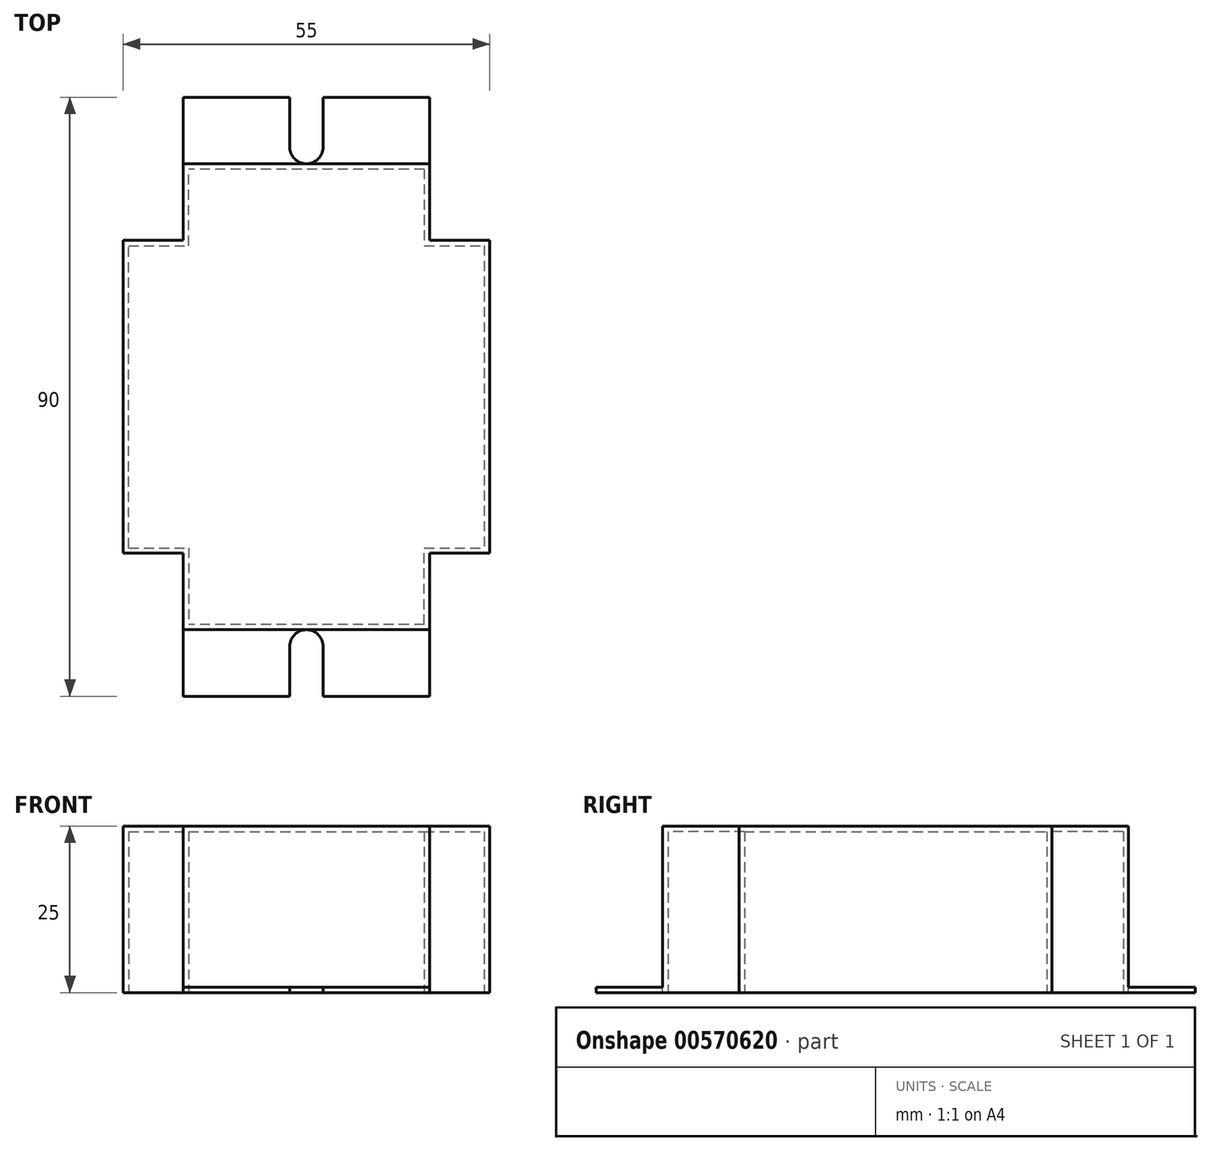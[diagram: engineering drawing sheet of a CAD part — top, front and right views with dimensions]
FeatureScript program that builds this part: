
annotation { "Feature Type Name" : "Feature", "Feature Type Description" : "" }
export const myFeature = defineFeature(function(context is Context, id is Id, definition is map)
    precondition{}
    {
        {
            var Q0;
            Q0=qCreatedBy(makeId("Top.planeOp"),FACE);
            var sketch = newSketch(context, id + "F0", { "sketchPlane" : qUnion([Q0])});
            skLineSegment(sketch, "E0", {"start": v(-33.6, -23.5) * mm, "end": v(-33.6, 23.5) * mm});
            skLineSegment(sketch, "E1", {"start": v(-33.6, 23.5) * mm, "end": v(-24.6, 23.5) * mm});
            skLineSegment(sketch, "E2", {"start": v(-24.6, 23.5) * mm, "end": v(-24.6, 35) * mm});
            skLineSegment(sketch, "E3", {"start": v(-24.6, 35) * mm, "end": v(12.4, 35) * mm});
            skLineSegment(sketch, "E4", {"start": v(12.4, 35) * mm, "end": v(12.4, 23.5) * mm});
            skLineSegment(sketch, "E5", {"start": v(12.4, 23.5) * mm, "end": v(21.4, 23.5) * mm});
            skLineSegment(sketch, "E6", {"start": v(21.4, 23.5) * mm, "end": v(21.4, -23.5) * mm});
            skLineSegment(sketch, "E7", {"start": v(35.03, 0) * mm, "end": v(-45.05, 0) * mm, "construction": true});
            skLineSegment(sketch, "E8.MirrorCS", {"start": v(-24.6, -35) * mm, "end": v(12.4, -35) * mm});
            skLineSegment(sketch, "E9.MirrorCS", {"start": v(12.4, -35) * mm, "end": v(12.4, -23.5) * mm});
            skLineSegment(sketch, "E10.MirrorCS", {"start": v(-33.6, -23.5) * mm, "end": v(-24.6, -23.5) * mm});
            skLineSegment(sketch, "E11.MirrorCS", {"start": v(-24.6, -23.5) * mm, "end": v(-24.6, -35) * mm});
            skLineSegment(sketch, "E12.MirrorCS", {"start": v(12.4, -23.5) * mm, "end": v(21.4, -23.5) * mm});
            skPoint(sketch, "E13.orphan", {"position": v(-33.6, 0) * mm});
            skPoint(sketch, "E14.orphan", {"position": v(21.4, 0) * mm});
            skSolve(sketch);
        }
        {
            var Q0;
            Q0=makeQuery(id+"F0.imprint","IMPRINT",FACE,{"disambiguationData":[TD([[makeQuery(id+"F0.imprint","IMPRINT",EDGE,{"derivedFrom":sQuery(id+"F0.wireOp",EDGE,"E0")}),-1.0]])]});
            extrude(context, id + "F1", {"entities" : qUnion([Q0]), "depth" : 25 * mm, "offsetDistance" : 25 * mm});
        }
        {
            var Q0;
            Q0=makeQuery(id+"F1.opExtrude","SWEPT_FACE",FACE,{"disambiguationData":[OSD([sQuery(id+"F0.wireOp",EDGE,"E8.MirrorCS")])]});
            var sketch = newSketch(context, id + "F2", { "sketchPlane" : qUnion([Q0])});
            skLineSegment(sketch, "E15.bottom", {"start": v(12.4, 0) * mm, "end": v(-24.6, 0) * mm});
            skLineSegment(sketch, "E15.top", {"start": v(12.4, 0.8) * mm, "end": v(-24.6, 0.8) * mm});
            skLineSegment(sketch, "E15.left", {"start": v(12.4, 0) * mm, "end": v(12.4, 0.8) * mm});
            skLineSegment(sketch, "E15.right", {"start": v(-24.6, 0) * mm, "end": v(-24.6, 0.8) * mm});
            skSolve(sketch);
        }
        {
            var Q0;
            Q0 = qSketchRegion(id + "F2", true);
            extrude(context, id + "F3", {"entities" : qUnion([Q0]), "operationType" : NewBodyOperationType.ADD, "depth" : 10 * mm, "offsetDistance" : 25 * mm});
        }
        {
            var Q0;
            Q0=makeQuery(id+"F1.opExtrude","SWEPT_FACE",FACE,{"disambiguationData":[OSD([sQuery(id+"F0.wireOp",EDGE,"E3")])]});
            var sketch = newSketch(context, id + "F4", { "sketchPlane" : qUnion([Q0])});
            skLineSegment(sketch, "E16.bottom", {"start": v(-12.4, 0) * mm, "end": v(24.6, 0) * mm});
            skLineSegment(sketch, "E16.top", {"start": v(-12.4, 0.8) * mm, "end": v(24.6, 0.8) * mm});
            skLineSegment(sketch, "E16.left", {"start": v(-12.4, 0) * mm, "end": v(-12.4, 0.8) * mm});
            skLineSegment(sketch, "E16.right", {"start": v(24.6, 0) * mm, "end": v(24.6, 0.8) * mm});
            skSolve(sketch);
        }
        {
            var Q0;
            Q0 = qSketchRegion(id + "F4", true);
            extrude(context, id + "F5", {"entities" : qUnion([Q0]), "operationType" : NewBodyOperationType.ADD, "depth" : 10 * mm, "offsetDistance" : 25 * mm});
        }
        {
            var Q0;
            Q0=makeQuery(id+"F5.boolean.opBoolean","MERGE",FACE,{"derivedFrom":[makeQuery(id+"F3.boolean.opBoolean","MERGE",FACE,{"derivedFrom":[makeQuery(id+"F1.opExtrude","CAP_FACE",FACE,{"disambiguationData":[OSD([sQuery(id+"F0.wireOp",EDGE,"E0"),sQuery(id+"F0.wireOp",EDGE,"E1"),sQuery(id+"F0.wireOp",EDGE,"E2"),sQuery(id+"F0.wireOp",EDGE,"E3"),sQuery(id+"F0.wireOp",EDGE,"E4"),sQuery(id+"F0.wireOp",EDGE,"E5"),sQuery(id+"F0.wireOp",EDGE,"E6"),sQuery(id+"F0.wireOp",EDGE,"E8.MirrorCS"),sQuery(id+"F0.wireOp",EDGE,"E9.MirrorCS"),sQuery(id+"F0.wireOp",EDGE,"E10.MirrorCS"),sQuery(id+"F0.wireOp",EDGE,"E11.MirrorCS"),sQuery(id+"F0.wireOp",EDGE,"E12.MirrorCS")])],"isStart":true}),makeQuery(id+"F3.opExtrude","SWEPT_FACE",FACE,{"disambiguationData":[OSD([sQuery(id+"F2.wireOp",EDGE,"E15.bottom")])]})]}),makeQuery(id+"F5.opExtrude","SWEPT_FACE",FACE,{"disambiguationData":[OSD([sQuery(id+"F4.wireOp",EDGE,"E16.bottom")])]})]});
            shell(context, id + "F6", {"entities" : qUnion([Q0]), "thickness" : 0.8 * mm});
        }
        {
            var Q0;
            Q0=makeQuery(id+"F5.opExtrude","SWEPT_FACE",FACE,{"disambiguationData":[OSD([sQuery(id+"F4.wireOp",EDGE,"E16.top")])]});
            var sketch = newSketch(context, id + "F7", { "sketchPlane" : qUnion([Q0])});
            skLineSegment(sketch, "E17.top", {"start": v(-3.6, 45) * mm, "end": v(-8.6, 45) * mm});
            skLineSegment(sketch, "E17.left", {"start": v(-3.6, 37.5) * mm, "end": v(-3.6, 45) * mm});
            skLineSegment(sketch, "E17.right", {"start": v(-8.6, 37.5) * mm, "end": v(-8.6, 45) * mm});
            skArc(sketch, "E18", {"start": v(-8.6, 37.5) * mm, "mid": v(-6.1, 35) * mm, "end": v(-3.6, 37.5) * mm});
            skSolve(sketch);
        }
        {
            var Q0;
            Q0=makeQuery(id+"F3.opExtrude","SWEPT_FACE",FACE,{"disambiguationData":[OSD([sQuery(id+"F2.wireOp",EDGE,"E15.top")])]});
            var sketch = newSketch(context, id + "F8", { "sketchPlane" : qUnion([Q0])});
            skLineSegment(sketch, "E19.top", {"start": v(-8.6, -45) * mm, "end": v(-3.6, -45) * mm});
            skLineSegment(sketch, "E19.left", {"start": v(-8.6, -37.5) * mm, "end": v(-8.6, -45) * mm});
            skLineSegment(sketch, "E19.right", {"start": v(-3.6, -37.5) * mm, "end": v(-3.6, -45) * mm});
            skArc(sketch, "E20", {"start": v(-3.6, -37.5) * mm, "mid": v(-6.1, -35) * mm, "end": v(-8.6, -37.5) * mm});
            skSolve(sketch);
        }
        {
            var Q0;
            Q0=makeQuery(id+"F8.imprint","IMPRINT",FACE,{"disambiguationData":[TD([[makeQuery(id+"F8.imprint","IMPRINT",EDGE,{"derivedFrom":sQuery(id+"F8.wireOp",EDGE,"E19.top")}),-1.0]])]});
            var Q1;
            Q1=makeQuery(id+"F7.imprint","IMPRINT",FACE,{"disambiguationData":[TD([[makeQuery(id+"F7.imprint","IMPRINT",EDGE,{"derivedFrom":sQuery(id+"F7.wireOp",EDGE,"E17.top")}),1.0]])]});
            extrude(context, id + "F9", {"entities" : qUnion([Q0, Q1]), "operationType" : NewBodyOperationType.REMOVE, "oppositeDirection" : true, "depth" : 2 * mm, "offsetDistance" : 25 * mm});
        }
    });
